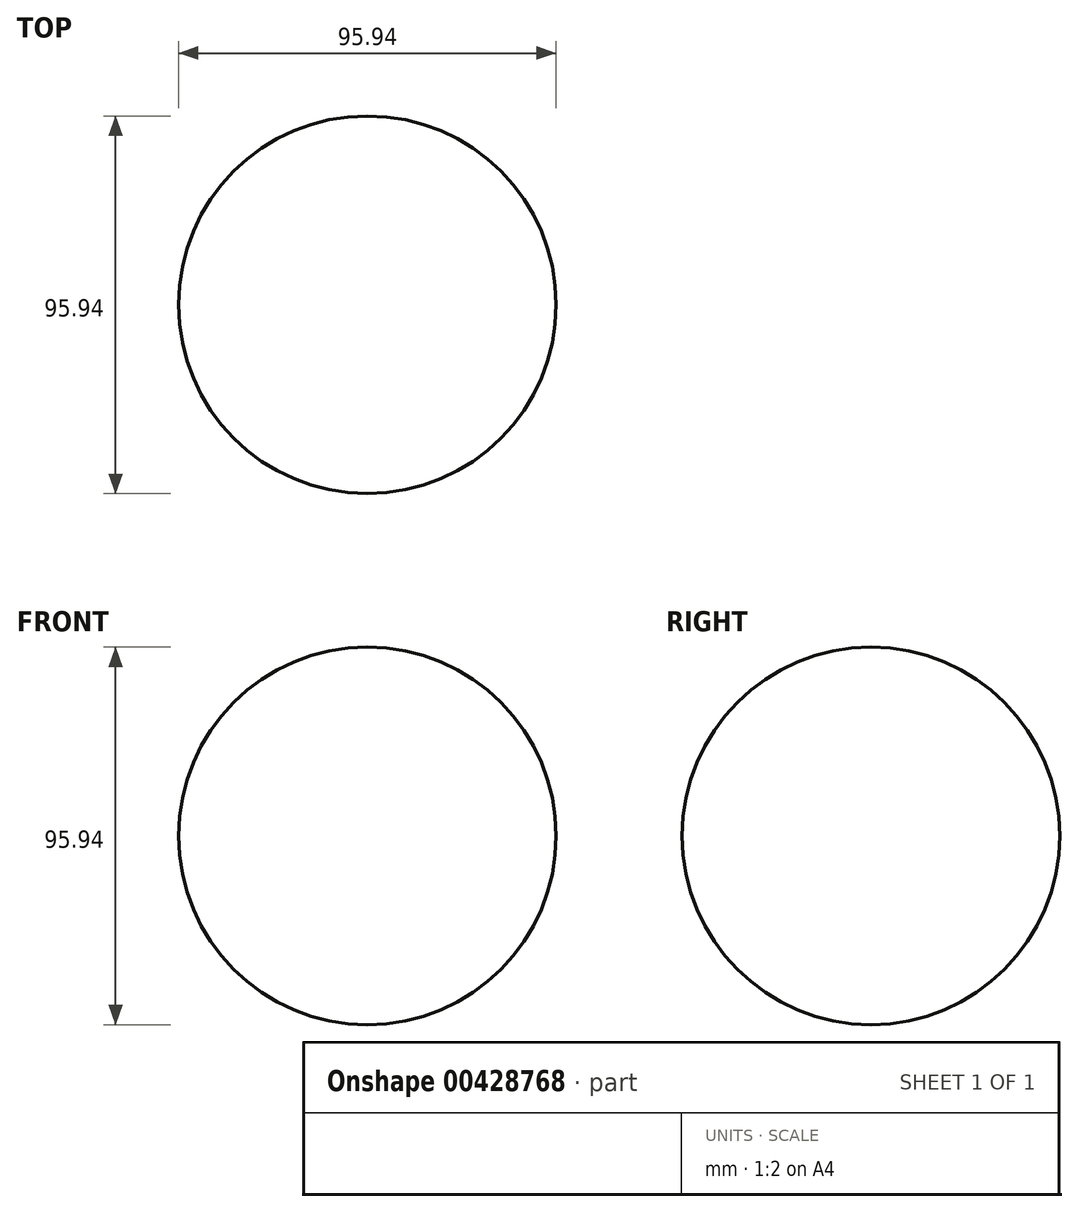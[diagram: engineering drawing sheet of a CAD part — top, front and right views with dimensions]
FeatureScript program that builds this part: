
annotation { "Feature Type Name" : "Feature", "Feature Type Description" : "" }
export const myFeature = defineFeature(function(context is Context, id is Id, definition is map)
    precondition{}
    {
        {
            var Q0;
            Q0=qCreatedBy(makeId("Top.planeOp"),FACE);
            var sketch = newSketch(context, id + "F0", { "sketchPlane" : qUnion([Q0])});
            skArc(sketch, "E0", {"start": v(0, -47.97) * mm, "mid": v(47.97, 0) * mm, "end": v(0, 47.97) * mm});
            skLineSegment(sketch, "E1", {"start": v(0, -47.97) * mm, "end": v(0, 47.97) * mm});
            skPoint(sketch, "E2.orphan", {"position": v(0, -65.96) * mm});
            skSolve(sketch);
        }
        {
            var Q0;
            Q0=makeQuery(id+"F0.imprint","IMPRINT",FACE,{"disambiguationData":[TD([[makeQuery(id+"F0.imprint","IMPRINT",EDGE,{"derivedFrom":sQuery(id+"F0.wireOp",EDGE,"E0")}),1.0]])]});
            var Q1;
            Q1=sQuery(id+"F0.wireOp",EDGE,"E1");
            revolve(context, id + "F1", {"entities" : qUnion([Q0]), "axis" : qUnion([Q1]), "revolveType" : RevolveType.FULL});
        }
    });
